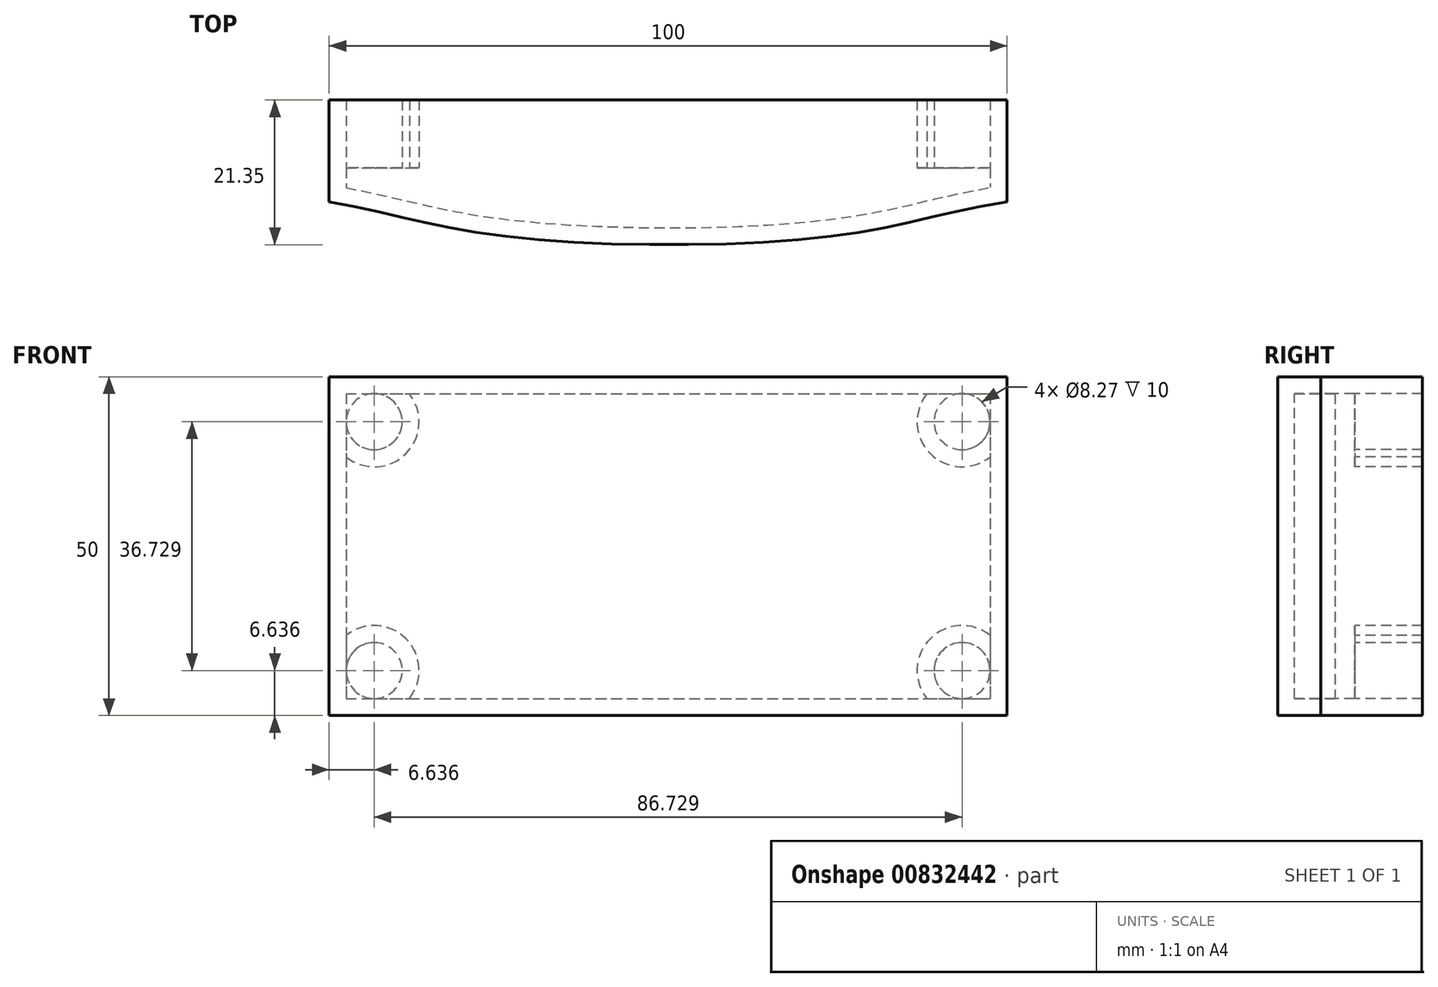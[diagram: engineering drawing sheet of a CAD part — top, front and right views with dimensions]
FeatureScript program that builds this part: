
annotation { "Feature Type Name" : "Feature", "Feature Type Description" : "" }
export const myFeature = defineFeature(function(context is Context, id is Id, definition is map)
    precondition{}
    {
        {
            var Q0;
            Q0=qCreatedBy(makeId("Top.planeOp"),FACE);
            var sketch = newSketch(context, id + "F0", { "sketchPlane" : qUnion([Q0])});
            skLineSegment(sketch, "E0.bottom", {"start": v(-50, 10) * mm, "end": v(50, 10) * mm});
            skLineSegment(sketch, "E0.left", {"start": v(-50, 10) * mm, "end": v(-50, -5) * mm});
            skLineSegment(sketch, "E0.right", {"start": v(50, 10) * mm, "end": v(50, -5) * mm});
            skFitSpline(sketch, "E1", {"points": [v(-50, -5) * mm, v(-25, -10) * mm, v(25, -10) * mm, v(50, -5) * mm], "startDerivative": vector(89.66, -15.53) * mm, "endDerivative": vector(96.85, 15.24) * mm});
            skPoint(sketch, "E2.orphan", {"position": v(-50, -10) * mm});
            skPoint(sketch, "E3.orphan", {"position": v(50, -10) * mm});
            skSolve(sketch);
        }
        {
            var Q0;
            Q0=makeQuery(id+"F0.imprint","IMPRINT",FACE,{"disambiguationData":[TD([[makeQuery(id+"F0.imprint","IMPRINT",EDGE,{"derivedFrom":sQuery(id+"F0.wireOp",EDGE,"E0.bottom")}),-1.0]])]});
            extrude(context, id + "F1", {"entities" : qUnion([Q0]), "endBound" : BoundingType.SYMMETRIC, "depth" : 50 * mm, "offsetDistance" : 25 * mm});
        }
        {
            var Q0;
            Q0=makeQuery(id+"F1.opExtrude","SWEPT_FACE",FACE,{"disambiguationData":[OSD([sQuery(id+"F0.wireOp",EDGE,"E0.bottom")])]});
            shell(context, id + "F2", {"entities" : qUnion([Q0]), "thickness" : 2.5 * mm});
        }
        {
            var Q0;
            Q0=qCreatedBy(makeId("Front.planeOp"),FACE);
            var sketch = newSketch(context, id + "F3", { "sketchPlane" : qUnion([Q0])});
            skCircle(sketch, "E4", {"center": v(43.36, -18.36) * mm, "radius": 4.14 * mm});
            skCircle(sketch, "E5", {"center": v(43.36, -18.36) * mm, "radius": 6.64 * mm});
            skSolve(sketch);
        }
        {
            var Q0;
            Q0 = qSketchRegion(id + "F3", true);
            var Q1;
            Q1=makeQuery(id+"F1.opExtrude","SWEPT_FACE",FACE,{"disambiguationData":[OSD([sQuery(id+"F0.wireOp",EDGE,"E0.bottom")])]});
            extrude(context, id + "F4", {"entities" : qUnion([Q0]), "endBound" : BoundingType.UP_TO_SURFACE, "oppositeDirection" : true, "depth" : 25 * mm, "endBoundEntityFace" : qUnion([Q1]), "offsetDistance" : 25 * mm});
        }
        {
            var Q0;
            Q0=makeQuery(id+"F4.opExtrude","SWEPT_BODY",BODY,{"disambiguationData":[OSD([sQuery(id+"F3.wireOp",EDGE,"E4"),sQuery(id+"F3.wireOp",EDGE,"E5")])]});
            var Q1;
            Q1=qCreatedBy(makeId("Top.planeOp"),FACE);
            mirror(context, id + "F5", {"entities" : qUnion([Q0]), "mirrorPlane" : qUnion([Q1])});
        }
        {
            var Q0;
            Q0=makeQuery(id+"F4.opExtrude","SWEPT_BODY",BODY,{"disambiguationData":[OSD([sQuery(id+"F3.wireOp",EDGE,"E4"),sQuery(id+"F3.wireOp",EDGE,"E5")])]});
            var Q1;
            Q1=makeQuery(id+"F5.opPattern","COPY",BODY,{"derivedFrom":makeQuery(id+"F4.opExtrude","SWEPT_BODY",BODY,{"disambiguationData":[OSD([sQuery(id+"F3.wireOp",EDGE,"E4"),sQuery(id+"F3.wireOp",EDGE,"E5")])]}),"instanceName":"1"});
            var Q2;
            Q2=qCreatedBy(makeId("Right.planeOp"),FACE);
            mirror(context, id + "F6", {"operationType" : NewBodyOperationType.ADD, "entities" : qUnion([Q0, Q1]), "mirrorPlane" : qUnion([Q2])});
        }
    });
